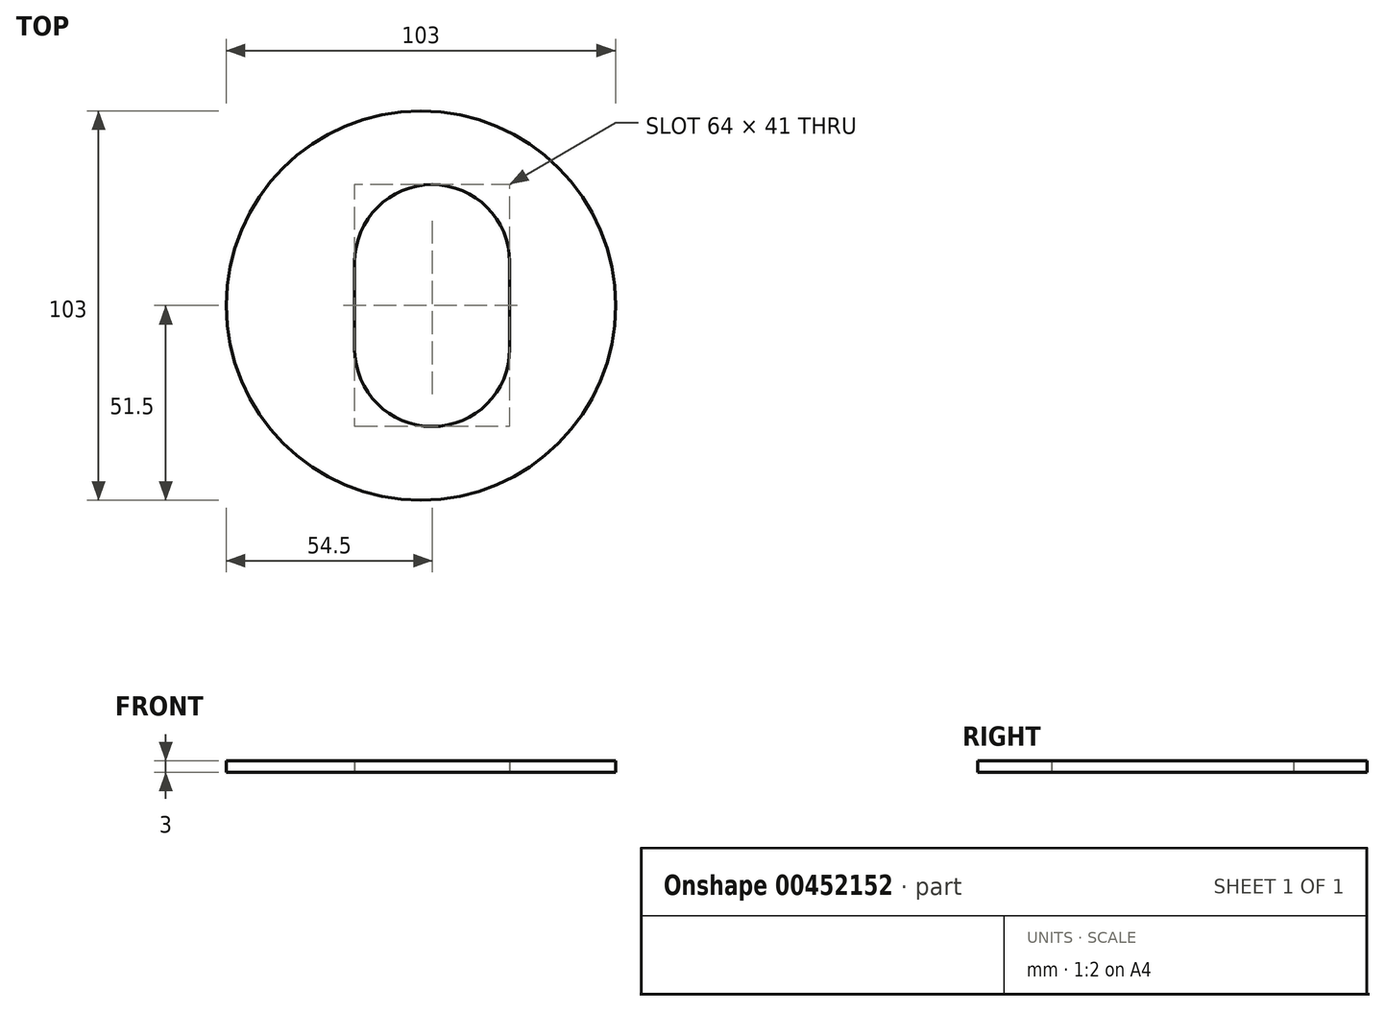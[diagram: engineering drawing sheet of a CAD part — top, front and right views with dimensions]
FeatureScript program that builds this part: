
annotation { "Feature Type Name" : "Feature", "Feature Type Description" : "" }
export const myFeature = defineFeature(function(context is Context, id is Id, definition is map)
    precondition{}
    {
        {
            var Q0;
            Q0=qCreatedBy(makeId("Top.planeOp"),FACE);
            var sketch = newSketch(context, id + "F0", { "sketchPlane" : qUnion([Q0])});
            skCircle(sketch, "E0", {"center": v(0, 0) * mm, "radius": 51.5 * mm});
            skLineSegment(sketch, "E1", {"start": v(-105.3, 0) * mm, "end": v(77.47, 0) * mm, "construction": true});
            skLineSegment(sketch, "E2.bottom", {"start": v(3, -32) * mm, "end": v(3, -32) * mm});
            skLineSegment(sketch, "E2.top", {"start": v(3, 32) * mm, "end": v(3, 32) * mm});
            skLineSegment(sketch, "E2.left", {"start": v(23.5, -11.5) * mm, "end": v(23.5, 11.5) * mm});
            skLineSegment(sketch, "E2.right", {"start": v(-17.5, -11.5) * mm, "end": v(-17.5, 11.5) * mm});
            skPoint(sketch, "E2.middle", {"position": v(3, 0) * mm});
            skPoint(sketch, "E3.visualSharp", {"position": v(-17.5, 32) * mm});
            skArc(sketch, "E3.filletArc", {"start": v(3, 32) * mm, "mid": v(-11.5, 26) * mm, "end": v(-17.5, 11.5) * mm});
            skPoint(sketch, "E4.visualSharp", {"position": v(23.5, 32) * mm});
            skArc(sketch, "E4.filletArc", {"start": v(23.5, 11.5) * mm, "mid": v(17.5, 26) * mm, "end": v(3, 32) * mm});
            skPoint(sketch, "E5.visualSharp", {"position": v(23.5, -32) * mm});
            skArc(sketch, "E5.filletArc", {"start": v(3, -32) * mm, "mid": v(17.5, -26) * mm, "end": v(23.5, -11.5) * mm});
            skPoint(sketch, "E6.visualSharp", {"position": v(-17.5, -32) * mm});
            skArc(sketch, "E6.filletArc", {"start": v(-17.5, -11.5) * mm, "mid": v(-11.5, -26) * mm, "end": v(3, -32) * mm});
            skSolve(sketch);
        }
        {
            var Q0;
            Q0=makeQuery(id+"F0.imprint","IMPRINT",FACE,{"disambiguationData":[TD([[makeQuery(id+"F0.imprint","IMPRINT",EDGE,{"derivedFrom":sQuery(id+"F0.wireOp",EDGE,"E0")}),1.0]])]});
            extrude(context, id + "F1", {"entities" : qUnion([Q0]), "depth" : 3 * mm, "offsetDistance" : 25 * mm});
        }
    });
